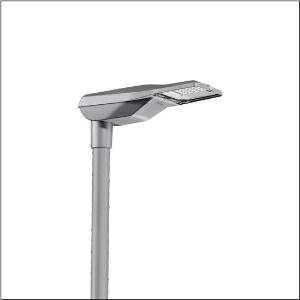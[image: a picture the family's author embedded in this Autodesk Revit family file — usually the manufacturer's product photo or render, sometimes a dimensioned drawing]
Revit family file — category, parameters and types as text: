
# Revit family: streetlight_sl_21_iq_micro___st1_0ab_5xe1m31g08cb_01f6
name_source: partatom
category: Lighting Fixtures
units: mm (PartAtom-declared; Revit-internal decimal feet)

## family parameters
Cut with Voids When Loaded = No
Host = Face
Light Source = No
Part Type = Normal
Room Calculation Point = No
Round Connector Dimension = Use Diameter
Shared = No

## types (1)
- --- (1 x LED, 2520 lm, 19.4 W, 3000K)
    Apparent Load = 19 VA
    CIE Flux Codes = 38 73 97 100 100
    Color Rendering = 70
    Color Temperature = 3000K
    Default Elevation = 1800 mm
    Description = Streetlight SL 21 iQ micro, mast luminaire, primary light control with lens, of PMMA, primary optical cover: cover, of toughened safety glass, transparent, light distribution: ST1.0aB, light emission: direct distribution, primary light characteristic: asymmetric, installation type: post-top, side-entry, LED, High Power LED, rated luminous flux: 2.520lm, luminous efficacy: 130lm/W, light colour: 730, colour temperature: 3000K, control gear: iQ Street-Remote, control: Street-Remote, Auto-Match, Temp-Guard, Lumen-Switch, Night-Set, Smart-Wire, Light-Fading, Desk-Remote (wireless, voltage-free reading and setting of iQ features in the workshop via application-optimized NFC function/RFID function), optimised constant luminous flux control (CLO 2.0), pre-setting: linear dimming characteristic, mains connection: 220..240V, AC, 50/60Hz, start of lifetime: 19W, end of service life: 20W, reduction: 10W, luminaire housing, of diecast aluminium, powder-coated, Siteco® metallic grey (DB 702S), corrosivity category C5 high according to DIN EN ISO 12944, please order mast flange separately, inclination adjustable: 0°, 5°, 10°, 15°, sealing non-destructively replaceable, multi-level sealing system, length: 528mm, width: 235mm, height: 110mm, mast flange for spigot size: 42mm (side-entry): 5XC10008XM4, 60/48mm (side-entry/post-top): 5XC10108XM2, 76/60mm (side-entry/post-top): 5XC10108XM1, protection rating (complete): IP66, insulation class (complete): insulation class II (safety insulation), certification: CE, ENEC, ENEC+, VDE, impact resistance: IK10, permissible operating ambient temperature for outdoor applications: -40..+50°C, standard-compliant lighting for roads and squares, packaging unit: 1 piece

Light Distribution: ST1.0aB
    Height = 110 mm
    Lamp = 1 x LED
    Lamp Light Flux = 2520 lm
    Lamp Power = 19.4 W
    Lamp count = 1
    Length = 528 mm
    Luminous efficacy = 130 lm/W
    Manufacturer = Siteco
    ModVariant = No
    Model = 5XE1M31G08CB
    Number of Poles = 1
    OnlyDefault = Yes
    Power Factor = 1
    Product Name = Streetlight SL 21 iQ micro | ST1.0aB
    Product group = mast luminaire | pylon top
    ProductGroupID = 6100
    Protection Class = Protection class II
    Protection Degree = IP 66
    RLX_Detail_Level = 1
    RLX_Emergency_Light_Flux = 0 lm
    RLX_Emergency_Type = 0
    RLX_Emergency_Type_DB = No
    RlxData = <blob elided: 99289 chars, md5=40060ae8>
    Socket = socket
    Standby Power = 0 W
    System Light Flux = 2520 lm
    System Power = 19 W
    Type Comments = factory setting: luminous flux: 100 % | dim-lin: 254 | 387 mA
    Type Image = l_1006881.jpg
    URL = http://relux.com
    VarID = @adj_141421
    Voltage = 0 V
    Weight = 0.00 kg
    Width = 235 mm

## geometry (parser evidence)
native form markers: Blend x4, Sweep x10
no freeform markers — native parametric forms only
